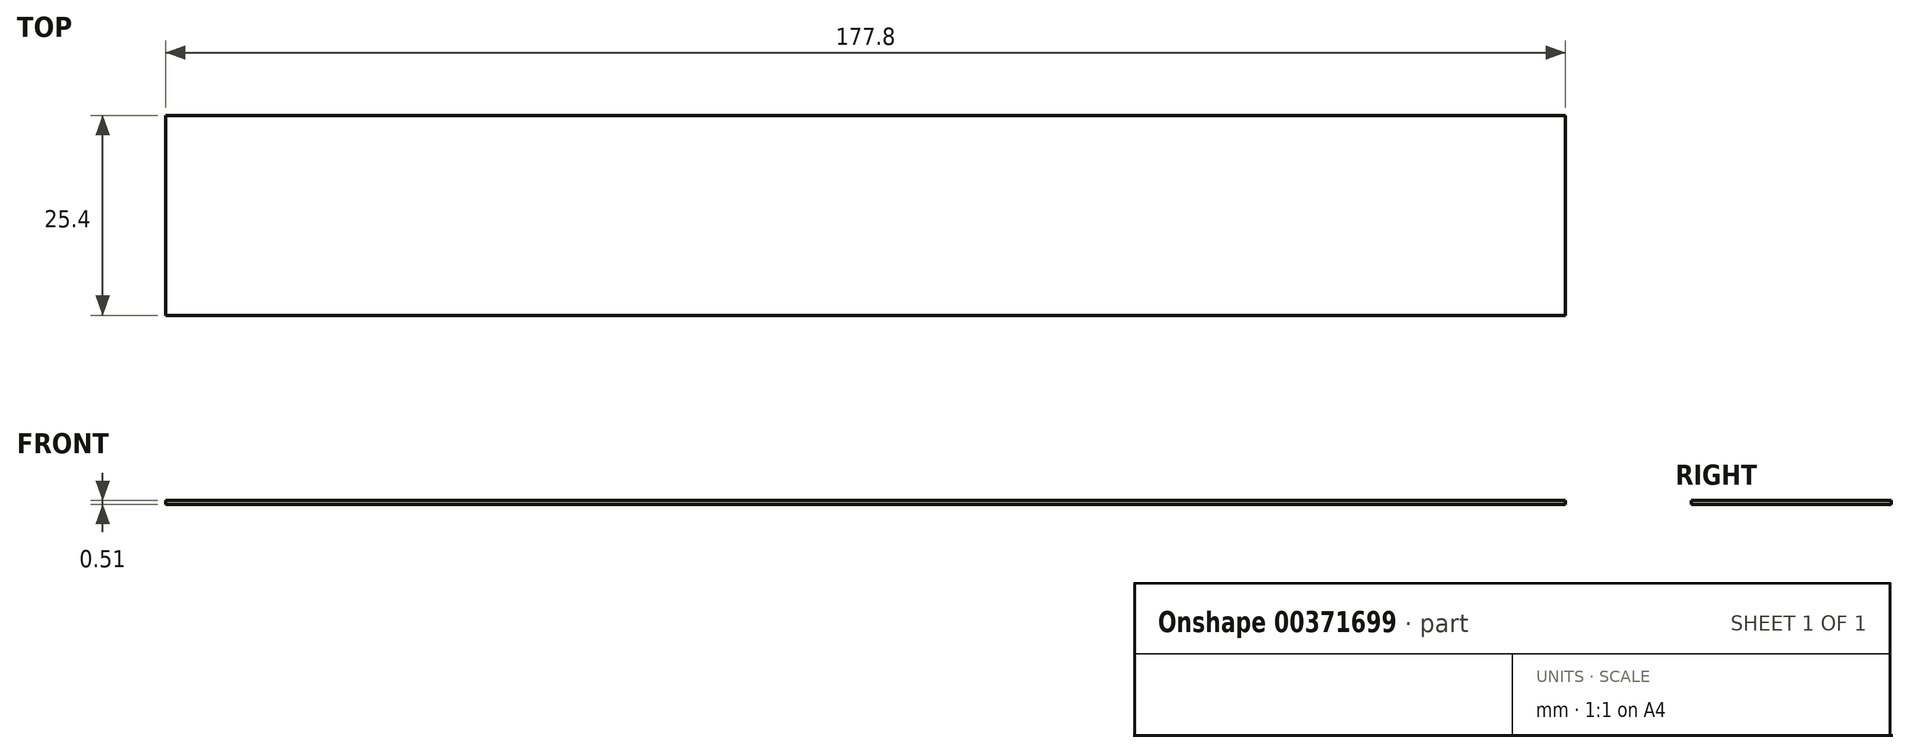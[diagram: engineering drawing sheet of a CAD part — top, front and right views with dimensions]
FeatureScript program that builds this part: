
annotation { "Feature Type Name" : "Feature", "Feature Type Description" : "" }
export const myFeature = defineFeature(function(context is Context, id is Id, definition is map)
    precondition{}
    {
        {
            var Q0;
            Q0=qCreatedBy(makeId("Top.planeOp"),FACE);
            var sketch = newSketch(context, id + "F0", { "sketchPlane" : qUnion([Q0])});
            skLineSegment(sketch, "E0.bottom", {"start": v(88.9, -12.7) * mm, "end": v(-88.9, -12.7) * mm});
            skLineSegment(sketch, "E0.top", {"start": v(88.9, 12.7) * mm, "end": v(-88.9, 12.7) * mm});
            skLineSegment(sketch, "E0.left", {"start": v(88.9, -12.7) * mm, "end": v(88.9, 12.7) * mm});
            skLineSegment(sketch, "E0.right", {"start": v(-88.9, -12.7) * mm, "end": v(-88.9, 12.7) * mm});
            skPoint(sketch, "E0.middle", {"position": v(0, 0) * mm});
            skSolve(sketch);
        }
        {
            var Q0;
            Q0=makeQuery(id+"F0.imprint","IMPRINT",FACE,{"disambiguationData":[TD([[makeQuery(id+"F0.imprint","IMPRINT",EDGE,{"derivedFrom":sQuery(id+"F0.wireOp",EDGE,"E0.bottom")}),-1.0]])]});
            extrude(context, id + "F1", {"entities" : qUnion([Q0]), "depth" : 0.5 * mm, "offsetDistance" : 25.4 * mm});
        }
    });
